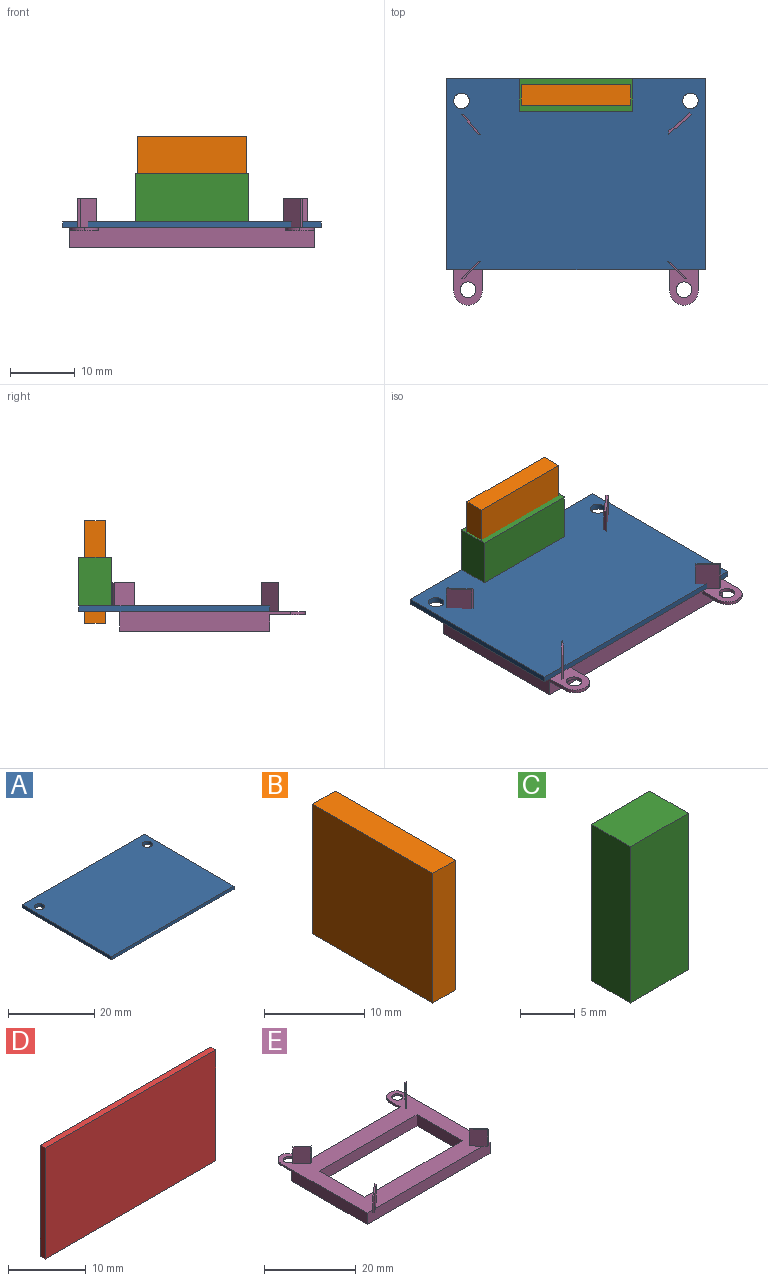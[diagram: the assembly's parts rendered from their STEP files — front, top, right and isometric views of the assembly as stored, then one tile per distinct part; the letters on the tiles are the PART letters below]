
ASSEMBLY  parts=5 mates=4
PART A: 8 faces, bbox 40x29.5x0.9 mm
  f0: plane 40x0.9mm, normal (0,1,0), area 36mm2, adj f1,f3,f4,f5
  f1: plane 29.5x0.9mm, normal (-1,0,0), area 26.5mm2, adj f0,f2,f4,f5
  f2: plane 40x0.9mm, normal (0,-1,0), area 36mm2, adj f1,f3,f4,f5
  f3: plane 29.5x0.9mm, normal (1,0,0), area 26.5mm2, adj f0,f2,f4,f5
  f4: plane 40x29.5mm, normal (0,0,1), area 1171mm2, adj f0,f1,f2,f3,f6,f7
  f5: plane 40x29.5mm, normal (0,0,-1), area 1171mm2, adj f0,f1,f2,f3,f6,f7
  f6: cylinder r=1.2mm len=2.4mm, axis (0,0,1), area 6.8mm2, adj f4,f5
  f7: cylinder r=1.2mm len=2.4mm, axis (0,0,1), area 6.8mm2, adj f4,f5
PART B: 6 faces, bbox 3.2x16.9x15.8 mm
  f0: plane 16.9x15.8mm, normal (-1,0,0), area 267mm2, adj f1,f3,f4,f5
  f1: plane 16.9x3.2mm, normal (0,0,-1), area 54.1mm2, adj f0,f2,f4,f5
  f2: plane 16.9x15.8mm, normal (1,0,0), area 267mm2, adj f1,f3,f4,f5
  f3: plane 16.9x3.2mm, normal (0,0,1), area 54.1mm2, adj f0,f2,f4,f5
  f4: plane 15.8x3.2mm, normal (0,-1,0), area 50.6mm2, adj f0,f1,f2,f3
  f5: plane 15.8x3.2mm, normal (0,1,0), area 50.6mm2, adj f0,f1,f2,f3
PART C: 6 faces, bbox 7.5x5x17.5 mm
  f0: plane 7.5x5mm, normal (0,0,1), area 37.5mm2, adj f1,f3,f4,f5
  f1: plane 17.5x5mm, normal (-1,0,0), area 87.5mm2, adj f0,f2,f4,f5
  f2: plane 7.5x5mm, normal (0,0,-1), area 37.5mm2, adj f1,f3,f4,f5
  f3: plane 17.5x5mm, normal (1,0,0), area 87.5mm2, adj f0,f2,f4,f5
  f4: plane 17.5x7.5mm, normal (0,-1,0), area 131.2mm2, adj f0,f1,f2,f3
  f5: plane 17.5x7.5mm, normal (0,1,0), area 131.2mm2, adj f0,f1,f2,f3
PART D: 6 faces, bbox 31x0.9x17.5 mm
  f0: plane 31x0.9mm, normal (0,0,1), area 27.9mm2, adj f1,f3,f4,f5
  f1: plane 17.5x0.9mm, normal (-1,0,0), area 15.8mm2, adj f0,f2,f4,f5
  f2: plane 31x0.9mm, normal (0,0,-1), area 27.9mm2, adj f1,f3,f4,f5
  f3: plane 17.5x0.9mm, normal (1,0,0), area 15.8mm2, adj f0,f2,f4,f5
  f4: plane 31x17.5mm, normal (0,-1,0), area 542.5mm2, adj f0,f1,f2,f3
  f5: plane 31x17.5mm, normal (0,1,0), area 542.5mm2, adj f0,f1,f2,f3
PART E: 94 faces, bbox 37.8x29.7x7.5 mm
  f0: plane 37.8x3mm, normal (0,1,0), area 109mm2, adj f1,f2,f3,f5,f82,f83,f85,f86
  f1: plane 37.8x28.7mm, normal (0,0,1), area 491.3mm2, adj f0,f3,f4,f5,f8,f9,f10,f13
  f2: plane 37.8x23.2mm, normal (0,0,-1), area 326mm2, adj f0,f3,f4,f5,f28,f29,f30,f31
  f3: plane 26.5x3mm, normal (-1,0,0), area 71.3mm2, adj f0,f1,f2,f4,f83,f89
  f4: plane 37.8x3mm, normal (0,-1,0), area 113.4mm2, adj f1,f2,f3,f5,f6,f12
  f5: plane 26.5x3mm, normal (1,0,0), area 71.3mm2, adj f0,f1,f2,f4,f86,f90
  f6: plane 1.44x1.02mm, normal (0,0,-1), area 0.5mm2, adj f4,f7,f8,f10
  f7: plane 4.5x0.3mm, normal (-0.76,-0.65,0), area 1.8mm2, adj f6,f8,f10,f11
  f8: plane 4.5x3.22mm, normal (0.65,-0.76,0), area 19.1mm2, adj f1,f6,f7,f9,f11
  f9: plane 4.5x0.51mm, normal (1,0,0), area 2.3mm2, adj f1,f8,f10,f11
  f10: plane 4.5x3.47mm, normal (-0.65,0.76,0), area 20.6mm2, adj f1,f6,f7,f9,f11
  f11: plane 3.47x3.28mm, normal (0,0,1), area 1.7mm2, adj f7,f8,f9,f10
  f12: plane 0.96x0.72mm, normal (0,0,-1), area 0.2mm2, adj f4,f13,f14,f15
  f13: plane 4.5x2.98mm, normal (-0.76,-0.65,0), area 17.7mm2, adj f1,f12,f14,f16,f17
  f14: plane 4.5x0.34mm, normal (0,-1,0), area 1.5mm2, adj f12,f13,f15,f17
  f15: plane 4.5x2.98mm, normal (0.76,0.65,0), area 17.7mm2, adj f1,f12,f14,f16,f17
  f16: plane 4.5x0.34mm, normal (0,1,0), area 1.5mm2, adj f1,f13,f15,f17
  f17: plane 2.98x2.9mm, normal (0,0,1), area 1mm2, adj f13,f14,f15,f16
  f18: plane 4.5x0.35mm, normal (0,1,0), area 1.6mm2, adj f1,f19,f21,f22
  f19: plane 4.5x2.68mm, normal (-0.72,0.69,0), area 16.7mm2, adj f1,f18,f20,f22
  f20: plane 4.5x0.36mm, normal (0.02,-1,0), area 1.6mm2, adj f1,f19,f21,f22
  f21: plane 4.5x2.67mm, normal (0.72,-0.69,0), area 16.7mm2, adj f1,f18,f20,f22
  f22: plane 2.93x2.68mm, normal (0,0,1), area 0.9mm2, adj f18,f19,f20,f21
  f23: plane 4.5x0.28mm, normal (0.33,-0.94,0), area 1.3mm2, adj f1,f24,f26,f27
  f24: plane 4.5x2.69mm, normal (0.69,0.72,0), area 16.8mm2, adj f1,f23,f25,f27
  f25: plane 4.5x0.38mm, normal (0,1,0), area 1.7mm2, adj f1,f24,f26,f27
  f26: plane 4.5x2.79mm, normal (-0.69,-0.72,0), area 17.4mm2, adj f1,f23,f25,f27
  f27: plane 3.06x2.67mm, normal (0,0,1), area 1mm2, adj f23,f24,f25,f26
  f28: plane 30x3mm, normal (0,-1,0), area 90mm2, adj f1,f2,f29,f31
  f29: plane 13.9x3mm, normal (-1,0,0), area 41.7mm2, adj f1,f2,f28,f30
  f30: plane 30x3mm, normal (0,1,0), area 90mm2, adj f1,f2,f29,f31
  f31: plane 13.9x3mm, normal (1,0,0), area 41.7mm2, adj f1,f2,f28,f30
  f32: plane 1.02x0.05mm, normal (1,0,0), area 0.1mm2, adj f56,f62,f65,f71
  f33: plane 34.01x0.05mm, normal (0,-1,0), area 1.7mm2, adj f59,f63,f65,f67
  f34: plane 1.02x0.05mm, normal (-1,0,0), area 0.1mm2, adj f54,f58,f59,f68
  f35: plane 34.01x0.05mm, normal (0,1,0), area 1.7mm2, adj f54,f56,f57,f72
  f36: plane 34.01x1.02mm, normal (0,0,-1), area 34.8mm2, adj f57,f58,f62,f63
  f37: plane 1.02x0.05mm, normal (1,0,0), area 0.1mm2, adj f47,f51,f53,f80
  f38: plane 34.01x0.05mm, normal (0,-1,0), area 1.7mm2, adj f42,f46,f47,f79
  f39: plane 1.02x0.05mm, normal (-1,0,0), area 0.1mm2, adj f42,f44,f45,f75
  f40: plane 34.01x0.05mm, normal (0,1,0), area 1.7mm2, adj f44,f50,f53,f76
  f41: plane 34.01x1.02mm, normal (0,0,-1), area 34.8mm2, adj f45,f46,f50,f51
  f42: cylinder r=0.25mm len=0.25mm, axis (0,0,-1), area 0mm2, adj f38,f39,f43,f77
  f43: sphere r=0.25mm, area 0.1mm2, adj f42,f45,f46
  f44: cylinder r=0.25mm len=0.25mm, axis (0,0,1), area 0mm2, adj f39,f40,f48,f74
  f45: cylinder r=0.25mm len=1.02mm, axis (0,-1,0), area 0.4mm2, adj f39,f41,f43,f48
  f46: cylinder r=0.25mm len=34.01mm, axis (1,0,0), area 13.4mm2, adj f38,f41,f43,f49
  f47: cylinder r=0.25mm len=0.25mm, axis (0,0,1), area 0mm2, adj f37,f38,f49,f81
  f48: sphere r=0.25mm, area 0.1mm2, adj f44,f45,f50
  f49: sphere r=0.25mm, area 0.1mm2, adj f46,f47,f51
  f50: cylinder r=0.25mm len=34.01mm, axis (-1,0,0), area 13.4mm2, adj f40,f41,f48,f52
  f51: cylinder r=0.25mm len=1.02mm, axis (0,1,0), area 0.4mm2, adj f37,f41,f49,f52
  f52: sphere r=0.25mm, area 0.1mm2, adj f50,f51,f53
  f53: cylinder r=0.25mm len=0.25mm, axis (0,0,-1), area 0mm2, adj f37,f40,f52,f78
  f54: cylinder r=0.25mm len=0.25mm, axis (0,0,1), area 0mm2, adj f34,f35,f55,f70
  f55: sphere r=0.25mm, area 0.1mm2, adj f54,f57,f58
  f56: cylinder r=0.25mm len=0.25mm, axis (0,0,-1), area 0mm2, adj f32,f35,f60,f73
  f57: cylinder r=0.25mm len=34.01mm, axis (-1,0,0), area 13.4mm2, adj f35,f36,f55,f60
  f58: cylinder r=0.25mm len=1.02mm, axis (0,-1,0), area 0.4mm2, adj f34,f36,f55,f61
  f59: cylinder r=0.25mm len=0.25mm, axis (0,0,-1), area 0mm2, adj f33,f34,f61,f66
  f60: sphere r=0.25mm, area 0.1mm2, adj f56,f57,f62
  f61: sphere r=0.25mm, area 0.1mm2, adj f58,f59,f63
  f62: cylinder r=0.25mm len=1.02mm, axis (0,1,0), area 0.4mm2, adj f32,f36,f60,f64
  f63: cylinder r=0.25mm len=34.01mm, axis (1,0,0), area 13.4mm2, adj f33,f36,f61,f64
  f64: sphere r=0.25mm, area 0.1mm2, adj f62,f63,f65
  f65: cylinder r=0.25mm len=0.25mm, axis (0,0,1), area 0mm2, adj f32,f33,f64,f69
  f66: torus R=0.45mm, axis (0,0,1), area 0.2mm2, adj f2,f59,f67,f68
  f67: cylinder r=0.2mm len=34.01mm, axis (1,0,0), area 10.7mm2, adj f2,f33,f66,f69
  f68: cylinder r=0.2mm len=1.02mm, axis (0,-1,0), area 0.3mm2, adj f2,f34,f66,f70
  f69: torus R=0.45mm, axis (0,0,1), area 0.2mm2, adj f2,f65,f67,f71
  f70: torus R=0.45mm, axis (0,0,1), area 0.2mm2, adj f2,f54,f68,f72
  f71: cylinder r=0.2mm len=1.02mm, axis (0,1,0), area 0.3mm2, adj f2,f32,f69,f73
  f72: cylinder r=0.2mm len=34.01mm, axis (-1,0,0), area 10.7mm2, adj f2,f35,f70,f73
  f73: torus R=0.45mm, axis (0,0,1), area 0.2mm2, adj f2,f56,f71,f72
  f74: torus R=0.45mm, axis (0,0,1), area 0.2mm2, adj f2,f44,f75,f76
  f75: cylinder r=0.2mm len=1.02mm, axis (0,-1,0), area 0.3mm2, adj f2,f39,f74,f77
  f76: cylinder r=0.2mm len=34.01mm, axis (-1,0,0), area 10.7mm2, adj f2,f40,f74,f78
  f77: torus R=0.45mm, axis (0,0,1), area 0.2mm2, adj f2,f42,f75,f79
  f78: torus R=0.45mm, axis (0,0,1), area 0.2mm2, adj f2,f53,f76,f80
  f79: cylinder r=0.2mm len=34.01mm, axis (1,0,0), area 10.7mm2, adj f2,f38,f77,f81
  f80: cylinder r=0.2mm len=1.02mm, axis (0,1,0), area 0.3mm2, adj f2,f37,f78,f81
  f81: torus R=0.45mm, axis (0,0,1), area 0.2mm2, adj f2,f47,f79,f80
  f82: plane 3.3x0.5mm, normal (1,0,0), area 1.7mm2, adj f0,f1,f83,f88
  f83: plane 5.5x4.4mm, normal (0,0,-1), area 17.6mm2, adj f0,f3,f82,f84,f88,f89,f93
  f84: plane 0.5x0mm, normal (0,1,0), area 0mm2, adj f1,f83,f88,f89
  f85: plane 3.3x0.5mm, normal (-1,0,0), area 1.7mm2, adj f0,f1,f86,f91
  f86: plane 5.5x4.4mm, normal (0,0,-1), area 17.6mm2, adj f0,f5,f85,f87,f90,f91,f92
  f87: plane 0.5x0mm, normal (0,1,0), area 0mm2, adj f1,f86,f90,f91
  f88: cylinder r=2.2mm len=2.2mm, axis (0,0,1), area 1.7mm2, adj f1,f82,f83,f84
  f89: cylinder r=2.2mm len=2.2mm, axis (0,0,-1), area 1.7mm2, adj f1,f3,f83,f84
  f90: cylinder r=2.2mm len=2.2mm, axis (0,0,1), area 1.7mm2, adj f1,f5,f86,f87
  f91: cylinder r=2.2mm len=2.2mm, axis (0,0,-1), area 1.7mm2, adj f1,f85,f86,f87
  f92: cylinder r=1.2mm len=2.4mm, axis (0,0,-1), area 3.8mm2, adj f1,f86
  f93: cylinder r=1.2mm len=2.4mm, axis (0,0,-1), area 3.8mm2, adj f1,f83
PLACE A t=(-1.57,-2.48,-13.82)mm
PLACE B rot(axis=(0,0,1),90deg) t=(9.98,22.92,0.22)mm
PLACE C rot(axis=(0.71,0,0.71),180deg) t=(9.68,22.02,-12.92)mm
PLACE D rot(axis=(1,0,0),90deg) t=(2.93,17.13,-14.65)mm
PLACE E rot(axis=(0,0,1),180deg) t=(37.33,20.72,-16.82)mm
MATE parallel C.f1 <-> A.f4  axis (0,0,-1) through (18.43,27.02,-12.92)mm
MATE parallel E.f1 <-> A.f5  axis (0,0,1) through (18.43,-2.48,-13.82)mm
MATE parallel B.f1 <-> C.f3  axis (0,0,-1) through (18.43,24.52,-15.58)mm
MATE parallel E.f2 <-> D.f4  axis (0,0,-1) through (18.43,2.17,-16.82)mm
